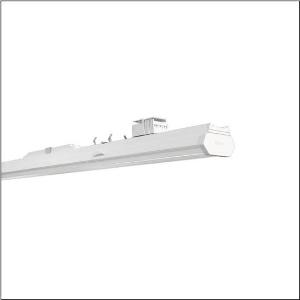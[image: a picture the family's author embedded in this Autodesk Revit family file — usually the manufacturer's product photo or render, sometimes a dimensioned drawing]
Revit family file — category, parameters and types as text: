
# Revit family: licross_r__11_protected_ho_51td12mn4f5m_c228
name_source: partatom
category: Lighting Fixtures
units: mm (PartAtom-declared; Revit-internal decimal feet)

## family parameters
Cut with Voids When Loaded = No
Host = Face
Light Source = No
Part Type = Normal
Room Calculation Point = No
Round Connector Dimension = Use Diameter
Shared = No

## types (1)
- --- (1 x LED, 15820 lm, 87.4 W, 4000K)
    Apparent Load = 87 VA
    CIE Flux Codes = 70 91 97 98 100
    Color Rendering = 80
    Color Temperature = 4000K
    Default Elevation = 1800 mm
    Description = Licross® 11 Protected HO, luminaire insert, of sheet steel, galvanised, coil coated, white, length: 1.500mm, width: 90mm, height: 101mm, LED rated luminous flux: 15.820lm, light colour: 840, control gear: ON/OFF Multilumen, with plug, 3-pole, with phase selection, mains connection: 220..240V, AC, 50/60Hz, rated input power: 87W, halogen-free wiring, primary light control with lens, of plastic, primary optical cover: cover, of PMMA, light emission: direct distribution, primary light characteristic: symmetric, protection rating (complete): IP54, insulation class (complete): insulation class I (protective earthing), certification: CE, ENEC, VDE, UKCA, protection symbol: D if used in an environment with non-conductive dust loads with corresponding accessories, impact resistance: IK06, permissible ambient temperature for indoor applications: -35..+35°C, corresponds to IFS (International Featured Standards) requirements for safety and quality in the food industry, reducing of maximum allowable ambient temperature of 5°C with ceiling mounting, LABS conformity tested according to VDMA 24364:2018-05, packaging unit: 1 piece
    Height = 92 mm
    Lamp = 1 x LED
    Lamp Light Flux = 15820 lm
    Lamp Power = 87.4 W
    Lamp count = 1
    Length = 1500 mm
    Luminous efficacy = 181 lm/W
    Manufacturer = Siteco
    ModVariant = No
    Model = 51TD12MN4F5M
    Mounting Place = Ceiling
    Mounting Type = Pendant
    Number of Poles = 1
    OnlyDefault = Yes
    Power Factor = 1
    Product Name = Licross® 11 Protected HO
    Product group = luminaire insert
    ProductGroupID = 901
    Protection Class = Protection class I
    Protection Degree = IP 54
    RLX_Detail_Level = 1
    RLX_Emergency_Light_Flux = 0 lm
    RLX_Emergency_Type = 0
    RLX_Emergency_Type_DB = No
    RlxData = <blob elided: 22101 chars, md5=f97e7c55>
    Socket = socket
    Standby Power = 0 W
    System Light Flux = 15820 lm
    System Power = 87 W
    Type Comments = factory setting: luminous flux: 100 % | (A | C | E) | 203 mA
    Type Image = l_1256145.jpg
    URL = http://relux.com
    VarID = @adj_081114
    Voltage = 0 V
    Weight = 0.00 kg
    Width = 88 mm

## geometry (parser evidence)
native form markers: Blend x4, Sweep x11
no freeform markers — native parametric forms only
